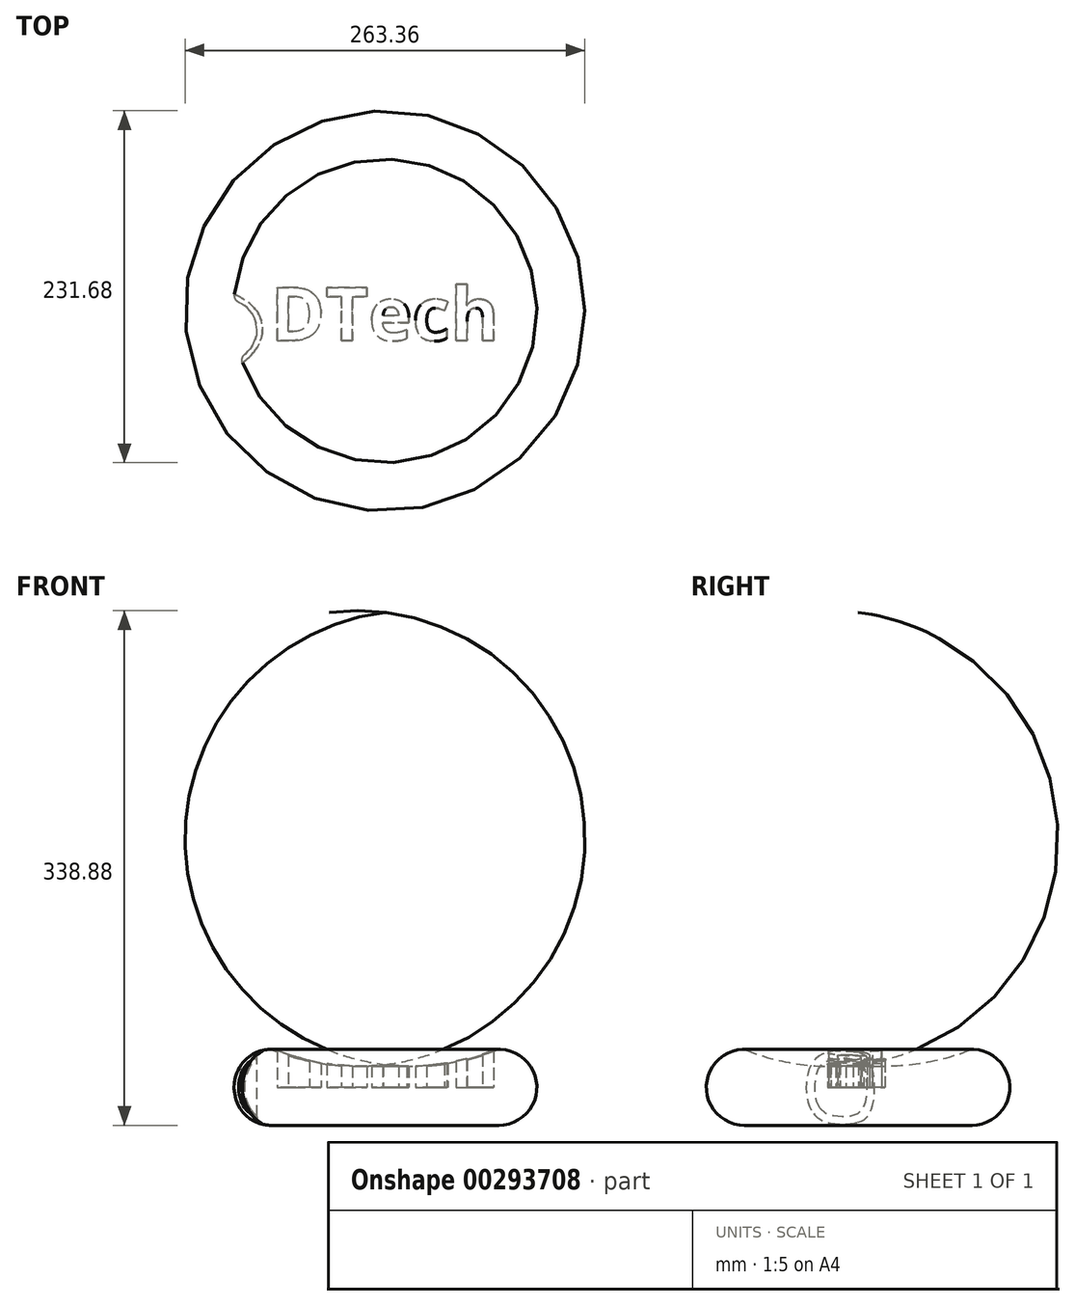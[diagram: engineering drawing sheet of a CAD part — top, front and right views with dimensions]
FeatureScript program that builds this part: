
annotation { "Feature Type Name" : "Feature", "Feature Type Description" : "" }
export const myFeature = defineFeature(function(context is Context, id is Id, definition is map)
    precondition{}
    {
        {
            var Q0;
            Q0=qCreatedBy(makeId("Front.planeOp"),FACE);
            var sketch = newSketch(context, id + "F0", { "sketchPlane" : qUnion([Q0])});
            skArc(sketch, "E0", {"start": v(-1.15, 24.97) * mm, "mid": v(-25, -0.58) * mm, "end": v(0, -25) * mm});
            skLineSegment(sketch, "E1", {"start": v(0, -25) * mm, "end": v(75, -25) * mm});
            skLineSegment(sketch, "E2", {"start": v(75, -25) * mm, "end": v(75, 15) * mm});
            skPoint(sketch, "E3", {"position": v(0, 25) * mm});
            skArc(sketch, "E4", {"start": v(0.94, 24.62) * mm, "mid": v(37.36, 15.13) * mm, "end": v(75, 15) * mm});
            skArc(sketch, "E5.filletArc", {"start": v(0.94, 24.62) * mm, "mid": v(-0.09, 24.9) * mm, "end": v(-1.15, 24.97) * mm});
            skSolve(sketch);
        }
        {
            var Q0;
            Q0 = qSketchRegion(id + "F0", true);
            var Q1;
            Q1=sQuery(id+"F0.wireOp",EDGE,"E2");
            revolve(context, id + "F1", {"entities" : qUnion([Q0]), "axis" : qUnion([Q1]), "revolveType" : RevolveType.FULL});
        }
        {
            var Q0;
            Q0=qCreatedBy(makeId("Top.planeOp"),FACE);
            var sketch = newSketch(context, id + "F2", { "sketchPlane" : qUnion([Q0])});
            skCircle(sketch, "E6", {"center": v(-29.37, -12.63) * mm, "radius": 20 * mm});
            skSolve(sketch);
        }
        {
            var Q0;
            Q0 = qSketchRegion(id + "F2", true);
            extrude(context, id + "F3", {"entities" : qUnion([Q0]), "operationType" : NewBodyOperationType.REMOVE, "endBound" : BoundingType.SYMMETRIC, "oppositeDirection" : true, "depth" : 100 * mm});
        }
        {
            var Q0;
            Q0=makeQuery(id+"F3.boolean.opBoolean","INTERSECT",EDGE,{"derivedFrom":[makeQuery(id+"F1.opRevolve","SWEPT_FACE",FACE,{"disambiguationData":[OSD([sQuery(id+"F0.wireOp",EDGE,"E0")])]}),makeQuery(id+"F3.opExtrude","SWEPT_FACE",FACE,{"disambiguationData":[OSD([sQuery(id+"F2.wireOp",EDGE,"E6")])]})]});
            fillet(context, id + "F4", {"entities" : qUnion([Q0]), "radius" : 5 * mm, "tangentPropagation" : true, "allowEdgeOverflow" : false});
        }
        {
            var Q0;
            Q0=qCreatedBy(makeId("Top.planeOp"),FACE);
            var sketch = newSketch(context, id + "F5", { "sketchPlane" : qUnion([Q0])});
            skText(sketch, "E7", { "text": "DTech", "fontName": "OpenSans-Bold.ttf"});
            const initialGuessF5  = {"E7": [-0.0004, -0.01953, 1, 0, 0.03516]};
            skSetInitialGuess(sketch, initialGuessF5);
            skSolve(sketch);
        }
        {
            var Q0;
            Q0 = qSketchRegion(id + "F5", true);
            extrude(context, id + "F6", {"entities" : qUnion([Q0]), "operationType" : NewBodyOperationType.REMOVE, "depth" : 50 * mm});
        }
    });
